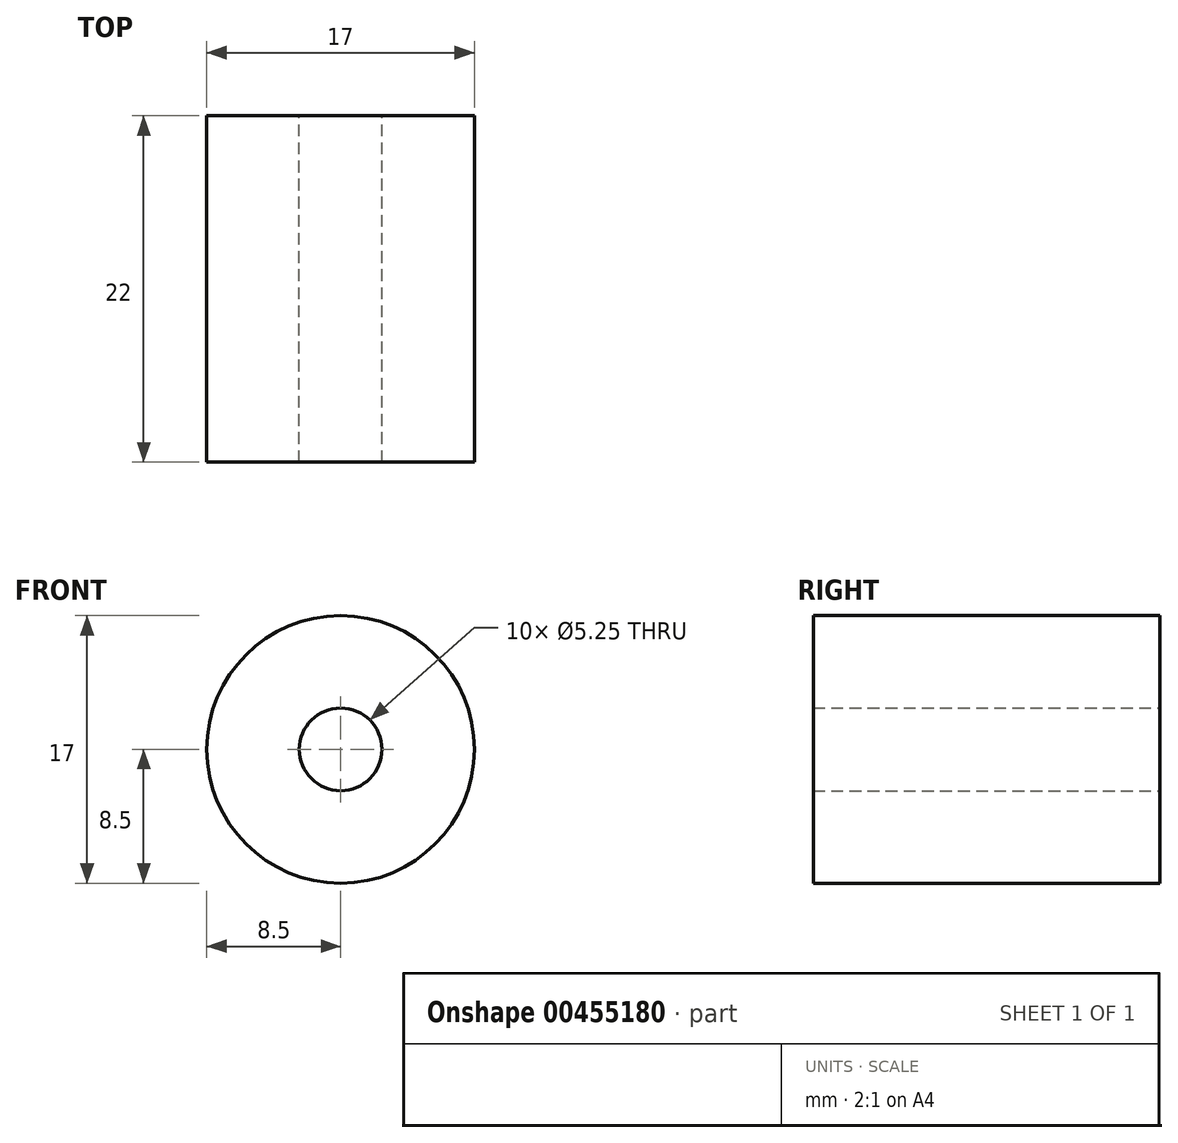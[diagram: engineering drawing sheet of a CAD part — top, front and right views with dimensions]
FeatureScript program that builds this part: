
annotation { "Feature Type Name" : "Feature", "Feature Type Description" : "" }
export const myFeature = defineFeature(function(context is Context, id is Id, definition is map)
    precondition{}
    {
        {
            var Q0;
            Q0=qCreatedBy(makeId("Front.planeOp"),FACE);
            var sketch = newSketch(context, id + "F0", { "sketchPlane" : qUnion([Q0])});
            skCircle(sketch, "E0", {"center": v(0, 0) * mm, "radius": 8.5 * mm});
            skCircle(sketch, "E1", {"center": v(0, 0) * mm, "radius": 2.62 * mm});
            skSolve(sketch);
        }
        {
            var Q0;
            Q0=makeQuery(id+"F0.imprint","IMPRINT",FACE,{"disambiguationData":[TD([[makeQuery(id+"F0.imprint","IMPRINT",EDGE,{"derivedFrom":sQuery(id+"F0.wireOp",EDGE,"E0")}),1.0]])]});
            extrude(context, id + "F1", {"entities" : qUnion([Q0]), "depth" : 22 * mm});
        }
    });
